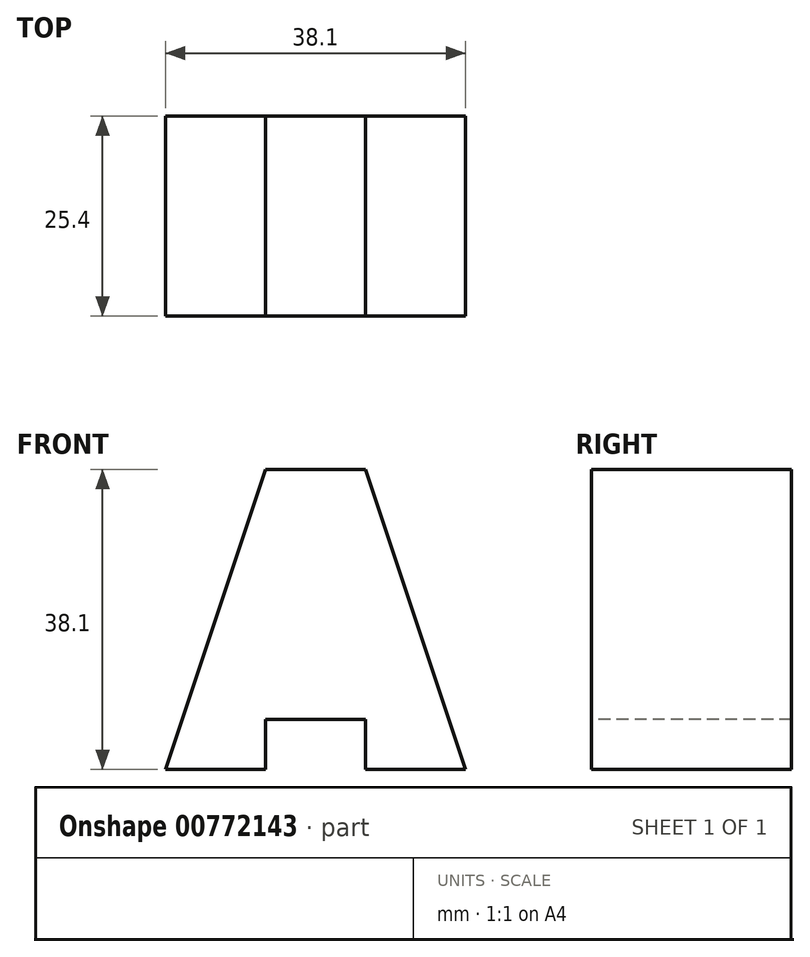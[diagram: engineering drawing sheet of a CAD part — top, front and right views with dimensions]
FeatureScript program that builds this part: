
annotation { "Feature Type Name" : "Feature", "Feature Type Description" : "" }
export const myFeature = defineFeature(function(context is Context, id is Id, definition is map)
    precondition{}
    {
        {
            var Q0;
            Q0=qCreatedBy(makeId("Front.planeOp"),FACE);
            var sketch = newSketch(context, id + "F0", { "sketchPlane" : qUnion([Q0])});
            skLineSegment(sketch, "E0", {"start": v(0, 0) * mm, "end": v(38.1, 0) * mm});
            skLineSegment(sketch, "E1", {"start": v(38.1, 0) * mm, "end": v(38.1, 38.1) * mm});
            skLineSegment(sketch, "E2", {"start": v(0, 0) * mm, "end": v(0, 38.1) * mm});
            skLineSegment(sketch, "E3", {"start": v(38.1, 38.1) * mm, "end": v(0, 38.1) * mm});
            skSolve(sketch);
        }
        {
            var Q0;
            Q0=makeQuery(id+"F0.imprint","IMPRINT",FACE,{"disambiguationData":[TD([[makeQuery(id+"F0.imprint","IMPRINT",EDGE,{"derivedFrom":sQuery(id+"F0.wireOp",EDGE,"E0")}),1.0]])]});
            extrude(context, id + "F1", {"entities" : qUnion([Q0]), "depth" : 25.4 * mm, "offsetDistance" : 25.4 * mm});
        }
        {
            var Q0;
            Q0=makeQuery(id+"F1.opExtrude","CAP_FACE",FACE,{"disambiguationData":[OSD([sQuery(id+"F0.wireOp",EDGE,"E0"),sQuery(id+"F0.wireOp",EDGE,"E1"),sQuery(id+"F0.wireOp",EDGE,"E2"),sQuery(id+"F0.wireOp",EDGE,"E3")])],"isStart":false});
            var sketch = newSketch(context, id + "F2", { "sketchPlane" : qUnion([Q0])});
            skLineSegment(sketch, "E4", {"start": v(19.05, 38.1) * mm, "end": v(12.7, 38.1) * mm});
            skLineSegment(sketch, "E5", {"start": v(19.05, 38.1) * mm, "end": v(25.4, 38.1) * mm});
            skLineSegment(sketch, "E6", {"start": v(12.7, 38.1) * mm, "end": v(0, 0) * mm});
            skLineSegment(sketch, "E7", {"start": v(25.4, 38.1) * mm, "end": v(38.1, 0) * mm});
            skSolve(sketch);
        }
        {
            var Q0;
            {var subQ0=sQuery(id+"F2.wireOp",EDGE,"E6");Q0=makeQuery(id+"F2.imprint","IMPRINT",FACE,{"disambiguationData":[TD([[makeQuery(id+"F2.imprint","IMPRINT",EDGE,{"derivedFrom":subQ0}),-1.0]])]});}
            var Q1;
            {var subQ0=sQuery(id+"F2.wireOp",EDGE,"E7");Q1=makeQuery(id+"F2.imprint","IMPRINT",FACE,{"disambiguationData":[TD([[makeQuery(id+"F2.imprint","IMPRINT",EDGE,{"derivedFrom":subQ0}),1.0]])]});}
            extrude(context, id + "F3", {"entities" : qUnion([Q0, Q1]), "operationType" : NewBodyOperationType.REMOVE, "oppositeDirection" : true, "depth" : 25.4 * mm, "offsetDistance" : 25.4 * mm});
        }
        {
            var Q0;
            Q0=makeQuery(id+"F1.opExtrude","CAP_FACE",FACE,{"disambiguationData":[OSD([sQuery(id+"F0.wireOp",EDGE,"E0"),sQuery(id+"F0.wireOp",EDGE,"E1"),sQuery(id+"F0.wireOp",EDGE,"E2"),sQuery(id+"F0.wireOp",EDGE,"E3")])],"isStart":false});
            var sketch = newSketch(context, id + "F4", { "sketchPlane" : qUnion([Q0])});
            skLineSegment(sketch, "E8", {"start": v(19.05, 0) * mm, "end": v(12.7, 0) * mm});
            skLineSegment(sketch, "E9", {"start": v(19.05, 0) * mm, "end": v(25.4, 0) * mm});
            skLineSegment(sketch, "E10", {"start": v(25.4, 0) * mm, "end": v(25.4, 6.35) * mm});
            skLineSegment(sketch, "E11", {"start": v(25.4, 6.35) * mm, "end": v(12.7, 6.35) * mm});
            skLineSegment(sketch, "E12", {"start": v(12.7, 0) * mm, "end": v(12.7, 6.35) * mm});
            skSolve(sketch);
        }
        {
            var Q0;
            Q0=makeQuery(id+"F4.imprint","IMPRINT",FACE,{"disambiguationData":[TD([[makeQuery(id+"F4.imprint","IMPRINT",EDGE,{"derivedFrom":sQuery(id+"F4.wireOp",EDGE,"E8")}),1.0]])]});
            extrude(context, id + "F5", {"entities" : qUnion([Q0]), "operationType" : NewBodyOperationType.REMOVE, "oppositeDirection" : true, "depth" : 25.4 * mm, "offsetDistance" : 25.4 * mm});
        }
    });
